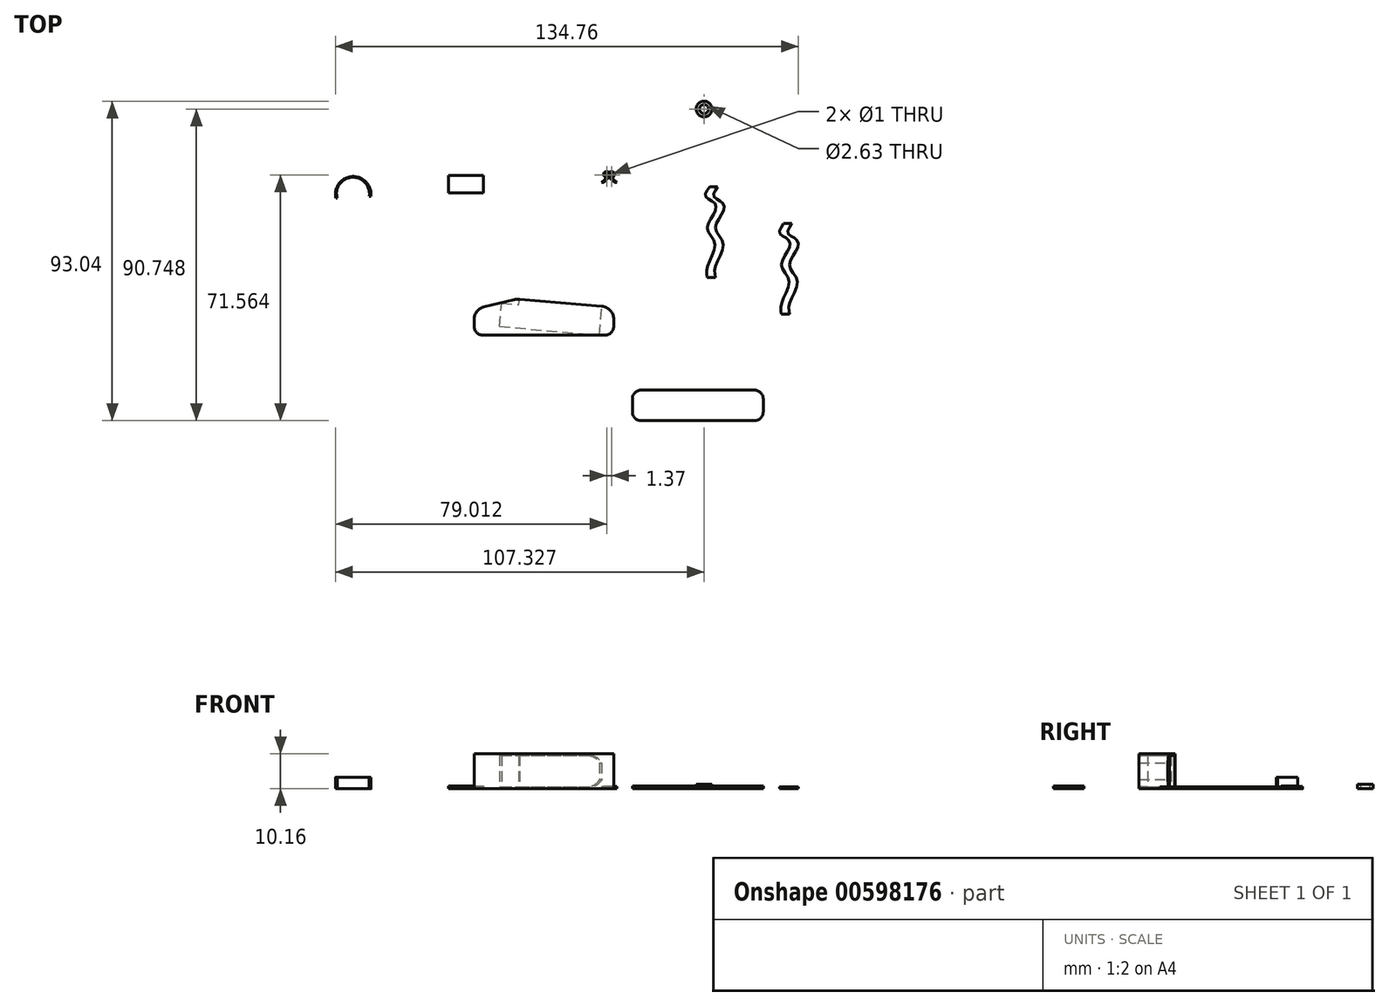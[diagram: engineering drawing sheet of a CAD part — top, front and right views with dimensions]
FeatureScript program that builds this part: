
annotation { "Feature Type Name" : "Feature", "Feature Type Description" : "" }
export const myFeature = defineFeature(function(context is Context, id is Id, definition is map)
    precondition{}
    {
        {
            var Q0;
            Q0=qCreatedBy(makeId("Top.planeOp"),FACE);
            var sketch = newSketch(context, id + "F0", { "sketchPlane" : qUnion([Q0])});
            skLineSegment(sketch, "E0", {"start": v(-27.73, 4.6) * mm, "end": v(-27.73, 2.54) * mm});
            skLineSegment(sketch, "E1", {"start": v(-25.19, 0) * mm, "end": v(10.37, 0) * mm});
            skLineSegment(sketch, "E2", {"start": v(-24.79, 8.3) * mm, "end": v(-16.13, 10.33) * mm});
            skLineSegment(sketch, "E3", {"start": v(-14.55, 10.45) * mm, "end": v(10.76, 8.28) * mm});
            skLineSegment(sketch, "E4", {"start": v(12.91, 4.6) * mm, "end": v(12.91, 2.54) * mm});
            skPoint(sketch, "E5.visualSharp", {"position": v(-27.73, 7.62) * mm});
            skArc(sketch, "E5.filletArc", {"start": v(-24.79, 8.3) * mm, "mid": v(-26.9, 6.97) * mm, "end": v(-27.73, 4.6) * mm});
            skPoint(sketch, "E6.visualSharp", {"position": v(-27.73, 0) * mm});
            skArc(sketch, "E6.filletArc", {"start": v(-27.73, 2.54) * mm, "mid": v(-26.98, 0.74) * mm, "end": v(-25.19, 0) * mm});
            skPoint(sketch, "E7.visualSharp", {"position": v(-15.36, 10.52) * mm});
            skArc(sketch, "E7.filletArc", {"start": v(-14.55, 10.45) * mm, "mid": v(-15.35, 10.45) * mm, "end": v(-16.14, 10.33) * mm});
            skPoint(sketch, "E8.visualSharp", {"position": v(12.91, 8.1) * mm});
            skArc(sketch, "E8.filletArc", {"start": v(12.91, 4.6) * mm, "mid": v(11.9, 7.18) * mm, "end": v(9.43, 8.4) * mm});
            skPoint(sketch, "E9.visualSharp", {"position": v(12.91, 0) * mm});
            skArc(sketch, "E9.filletArc", {"start": v(10.37, 0) * mm, "mid": v(12.17, 0.74) * mm, "end": v(12.91, 2.54) * mm});
            skSolve(sketch);
        }
        {
            var Q0;
            Q0=makeQuery(id+"F0.imprint","IMPRINT",FACE,{"disambiguationData":[TD([[makeQuery(id+"F0.imprint","IMPRINT",EDGE,{"derivedFrom":sQuery(id+"F0.wireOp",EDGE,"E0")}),1.0]])]});
            extrude(context, id + "F1", {"entities" : qUnion([Q0]), "depth" : 10.16 * mm, "offsetDistance" : 25.4 * mm});
        }
        {
            var Q0;
            Q0=makeQuery(id+"F1.opExtrude","SWEPT_FACE",FACE,{"disambiguationData":[OSD([sQuery(id+"F0.wireOp",EDGE,"E3")])]});
            var sketch = newSketch(context, id + "F2", { "sketchPlane" : qUnion([Q0])});
            skLineSegment(sketch, "E10.bottom", {"start": v(15.4, 9.65) * mm, "end": v(-5.25, 9.65) * mm});
            skLineSegment(sketch, "E10.top", {"start": v(15.4, 0.5) * mm, "end": v(-5.25, 0.5) * mm});
            skLineSegment(sketch, "E10.left", {"start": v(15.4, 9.65) * mm, "end": v(15.4, 0.5) * mm});
            skLineSegment(sketch, "E10.right", {"start": v(-9.06, 5.84) * mm, "end": v(-9.06, 4.32) * mm});
            skPoint(sketch, "E11.visualSharp", {"position": v(-9.06, 9.65) * mm});
            skArc(sketch, "E11.filletArc", {"start": v(-5.25, 9.65) * mm, "mid": v(-7.95, 8.54) * mm, "end": v(-9.06, 5.84) * mm});
            skPoint(sketch, "E12.visualSharp", {"position": v(-9.06, 0.5) * mm});
            skArc(sketch, "E12.filletArc", {"start": v(-9.06, 4.32) * mm, "mid": v(-7.95, 1.62) * mm, "end": v(-5.25, 0.5) * mm});
            skPoint(sketch, "E13.visualSharp", {"position": v(15.4, 0.5) * mm});
            skLineSegment(sketch, "E13.filletArc", {"start": v(15.4, 0.5) * mm, "end": v(15.4, 0.5) * mm});
            skPoint(sketch, "E14.visualSharp", {"position": v(15.4, 9.65) * mm});
            skLineSegment(sketch, "E14.filletArc", {"start": v(15.4, 9.65) * mm, "end": v(15.4, 9.65) * mm});
            skSolve(sketch);
        }
        {
            var Q0;
            {var subQ1=sQuery(id+"F2.wireOp",EDGE,"E10.bottom");Q0=makeQuery(id+"F2.imprint","IMPRINT",FACE,{"disambiguationData":[TD([[makeQuery(id+"F2.imprint","IMPRINT",EDGE,{"derivedFrom":subQ1}),1.0]])]});}
            extrude(context, id + "F3", {"entities" : qUnion([Q0]), "operationType" : NewBodyOperationType.REMOVE, "oppositeDirection" : true, "depth" : 8.38 * mm, "offsetDistance" : 25.4 * mm});
        }
        {
            var Q0;
            Q0=makeQuery(id+"F3.boolean.opBoolean","COPY",FACE,{"derivedFrom":makeQuery(id+"F3.opExtrude","SWEPT_FACE",FACE,{"disambiguationData":[OSD([sQuery(id+"F2.wireOp",EDGE,"E10.left")])]})});
            var sketch = newSketch(context, id + "F4", { "sketchPlane" : qUnion([Q0])});
            skLineSegment(sketch, "E15.bottom", {"start": v(7.63, 9.65) * mm, "end": v(0.79, 9.65) * mm});
            skLineSegment(sketch, "E15.top", {"start": v(7.63, 0.5) * mm, "end": v(0.79, 0.5) * mm});
            skLineSegment(sketch, "E15.left", {"start": v(7.63, 9.65) * mm, "end": v(7.63, 0.5) * mm});
            skLineSegment(sketch, "E15.right", {"start": v(0.79, 9.65) * mm, "end": v(0.79, 0.5) * mm});
            skSolve(sketch);
        }
        {
            var Q0;
            Q0=makeQuery(id+"F4.imprint","IMPRINT",FACE,{"disambiguationData":[TD([[makeQuery(id+"F4.imprint","IMPRINT",EDGE,{"derivedFrom":sQuery(id+"F4.wireOp",EDGE,"E15.bottom")}),-1.0]])]});
            extrude(context, id + "F5", {"entities" : qUnion([Q0]), "operationType" : NewBodyOperationType.REMOVE, "oppositeDirection" : true, "depth" : 5.08 * mm, "offsetDistance" : 25.4 * mm});
        }
        {
            var Q0;
            Q0=qCreatedBy(makeId("Top.planeOp"),FACE);
            var sketch = newSketch(context, id + "F6", { "sketchPlane" : qUnion([Q0])});
            skLineSegment(sketch, "E16.bottom", {"start": v(10.9, 47.63) * mm, "end": v(10.9, 47.63) * mm});
            skLineSegment(sketch, "E16.top", {"start": v(9.33, 44.42) * mm, "end": v(9.96, 44.42) * mm});
            skPoint(sketch, "E17.visualSharp", {"position": v(8.19, 47.63) * mm});
            skArc(sketch, "E17.filletArc", {"start": v(10.9, 47.63) * mm, "mid": v(10.66, 47.6) * mm, "end": v(10.44, 47.54) * mm});
            skLineSegment(sketch, "E18", {"start": v(9.96, 44.42) * mm, "end": v(11.58, 46.06) * mm});
            skLineSegment(sketch, "E19", {"start": v(9.33, 44.42) * mm, "end": v(10.33, 45.43) * mm});
            skLineSegment(sketch, "E20", {"start": v(10.3, 46.17) * mm, "end": v(10.21, 46.25) * mm});
            skPoint(sketch, "E21.visualSharp", {"position": v(9.67, 46.72) * mm});
            skArc(sketch, "E21.filletArc", {"start": v(10.44, 47.54) * mm, "mid": v(9.96, 46.96) * mm, "end": v(10.21, 46.25) * mm});
            skPoint(sketch, "E22.visualSharp", {"position": v(10.71, 45.82) * mm});
            skArc(sketch, "E22.filletArc", {"start": v(10.33, 45.43) * mm, "mid": v(10.48, 45.81) * mm, "end": v(10.3, 46.17) * mm});
            skPoint(sketch, "E23.visualSharp", {"position": v(11.45, 47.63) * mm});
            skArc(sketch, "E23.filletArc", {"start": v(11.58, 47.36) * mm, "mid": v(11.26, 47.56) * mm, "end": v(10.9, 47.63) * mm});
            skCircle(sketch, "E24", {"center": v(10.9, 46.66) * mm, "radius": 0.5 * mm});
            skArc(sketch, "E25.MirrorCS", {"start": v(12.26, 47.63) * mm, "mid": v(12.5, 47.6) * mm, "end": v(12.72, 47.54) * mm});
            skArc(sketch, "E26.MirrorCS", {"start": v(11.58, 47.36) * mm, "mid": v(11.9, 47.56) * mm, "end": v(12.26, 47.63) * mm});
            skArc(sketch, "E27.MirrorCS", {"start": v(12.72, 47.54) * mm, "mid": v(13.2, 46.96) * mm, "end": v(12.94, 46.25) * mm});
            skLineSegment(sketch, "E28.MirrorCS", {"start": v(12.85, 46.17) * mm, "end": v(12.94, 46.25) * mm});
            skCircle(sketch, "E29.MirrorC", {"center": v(12.26, 46.66) * mm, "radius": 0.5 * mm});
            skLineSegment(sketch, "E30.MirrorCS", {"start": v(13.82, 44.42) * mm, "end": v(12.82, 45.43) * mm});
            skLineSegment(sketch, "E31.MirrorCS", {"start": v(13.2, 44.42) * mm, "end": v(11.58, 46.06) * mm});
            skLineSegment(sketch, "E32.MirrorCS", {"start": v(13.82, 44.42) * mm, "end": v(13.2, 44.42) * mm});
            skArc(sketch, "E33.MirrorCS", {"start": v(12.82, 45.43) * mm, "mid": v(12.68, 45.81) * mm, "end": v(12.85, 46.17) * mm});
            skSolve(sketch);
        }
        {
            var Q0;
            Q0=makeQuery(id+"F6.imprint","IMPRINT",FACE,{"disambiguationData":[TD([[makeQuery(id+"F6.imprint","IMPRINT",EDGE,{"derivedFrom":sQuery(id+"F6.wireOp",EDGE,"E16.top")}),1.0]])]});
            extrude(context, id + "F7", {"entities" : qUnion([Q0]), "depth" : 0.64 * mm, "offsetDistance" : 25.4 * mm});
        }
        {
            var Q0;
            Q0=qCreatedBy(makeId("Top.planeOp"),FACE);
            var sketch = newSketch(context, id + "F8", { "sketchPlane" : qUnion([Q0])});
            skArc(sketch, "E34", {"start": v(-57.83, 40.38) * mm, "mid": v(-63.18, 46.21) * mm, "end": v(-68, 39.93) * mm});
            skArc(sketch, "E35", {"start": v(-58.3, 40.38) * mm, "mid": v(-63.24, 45.97) * mm, "end": v(-67.63, 39.93) * mm});
            skLineSegment(sketch, "E36", {"start": v(-68, 39.93) * mm, "end": v(-67.63, 39.93) * mm});
            skLineSegment(sketch, "E37", {"start": v(-58.3, 40.38) * mm, "end": v(-57.83, 40.38) * mm});
            skSolve(sketch);
        }
        {
            var Q0;
            Q0=makeQuery(id+"F8.imprint","IMPRINT",FACE,{"disambiguationData":[TD([[makeQuery(id+"F8.imprint","IMPRINT",EDGE,{"derivedFrom":sQuery(id+"F8.wireOp",EDGE,"E34")}),1.0]])]});
            extrude(context, id + "F9", {"entities" : qUnion([Q0]), "depth" : 3.3 * mm, "offsetDistance" : 25.4 * mm});
        }
        {
            var Q0;
            Q0=qCreatedBy(makeId("Top.planeOp"),FACE);
            var sketch = newSketch(context, id + "F10", { "sketchPlane" : qUnion([Q0])});
            skFitSpline(sketch, "E38", {"points": [v(40.82, 43.27) * mm, v(39.71, 40.38) * mm, v(42.15, 38.6) * mm, v(42.37, 35.94) * mm, v(40.15, 31.06) * mm, v(42.37, 26.62) * mm, v(40.15, 19.96) * mm, v(40.15, 16.86) * mm], "startDerivative": vector(-17.53, -25.97) * mm, "endDerivative": vector(4.73, -22) * mm});
            skFitSpline(sketch, "E39", {"points": [v(43.2, 43.27) * mm, v(42.09, 40.38) * mm, v(44.53, 38.6) * mm, v(44.75, 35.94) * mm, v(42.53, 31.06) * mm, v(44.75, 26.62) * mm, v(42.53, 19.96) * mm, v(42.53, 16.86) * mm], "startDerivative": vector(-17.53, -25.97) * mm, "endDerivative": vector(4.73, -22) * mm});
            skLineSegment(sketch, "E40", {"start": v(40.82, 43.27) * mm, "end": v(43.2, 43.27) * mm});
            skLineSegment(sketch, "E41", {"start": v(40.15, 16.86) * mm, "end": v(42.53, 16.86) * mm});
            skFitSpline(sketch, "E42", {"points": [v(62.4, 32.5) * mm, v(61.28, 29.61) * mm, v(63.73, 27.84) * mm, v(63.95, 25.17) * mm, v(61.73, 20.3) * mm, v(63.95, 15.85) * mm, v(61.73, 9.2) * mm, v(61.73, 6.09) * mm], "startDerivative": vector(-17.53, -25.97) * mm, "endDerivative": vector(4.73, -22) * mm});
            skFitSpline(sketch, "E43", {"points": [v(64.77, 32.5) * mm, v(63.66, 29.61) * mm, v(66.1, 27.84) * mm, v(66.33, 25.17) * mm, v(64.1, 20.3) * mm, v(66.33, 15.85) * mm, v(64.1, 9.2) * mm, v(64.1, 6.09) * mm], "startDerivative": vector(-17.53, -25.97) * mm, "endDerivative": vector(4.73, -22) * mm});
            skLineSegment(sketch, "E44", {"start": v(62.4, 32.5) * mm, "end": v(64.77, 32.5) * mm});
            skLineSegment(sketch, "E45", {"start": v(61.73, 6.09) * mm, "end": v(64.1, 6.09) * mm});
            skSolve(sketch);
        }
        {
            var Q0;
            Q0=makeQuery(id+"F10.imprint","IMPRINT",FACE,{"disambiguationData":[TD([[makeQuery(id+"F10.imprint","IMPRINT",EDGE,{"derivedFrom":sQuery(id+"F10.wireOp",EDGE,"E38")}),1.0]])]});
            extrude(context, id + "F11", {"entities" : qUnion([Q0]), "depth" : 0.5 * mm, "offsetDistance" : 25.4 * mm});
        }
        {
            var Q0;
            Q0 = qSketchRegion(id + "F10", true);
            extrude(context, id + "F12", {"entities" : qUnion([Q0]), "operationType" : NewBodyOperationType.ADD, "depth" : 0.5 * mm, "offsetDistance" : 25.4 * mm});
        }
        {
            var Q0;
            Q0=qCreatedBy(makeId("Top.planeOp"),FACE);
            var sketch = newSketch(context, id + "F13", { "sketchPlane" : qUnion([Q0])});
            skLineSegment(sketch, "E46.bottom", {"start": v(20.87, -16) * mm, "end": v(53.9, -16) * mm});
            skLineSegment(sketch, "E46.top", {"start": v(20.87, -24.9) * mm, "end": v(53.9, -24.9) * mm});
            skLineSegment(sketch, "E46.left", {"start": v(18.33, -18.55) * mm, "end": v(18.33, -22.36) * mm});
            skLineSegment(sketch, "E46.right", {"start": v(56.43, -18.55) * mm, "end": v(56.43, -22.36) * mm});
            skPoint(sketch, "E46.middle", {"position": v(37.38, -20.45) * mm});
            skPoint(sketch, "E47.visualSharp", {"position": v(18.33, -16) * mm});
            skArc(sketch, "E47.filletArc", {"start": v(20.87, -16) * mm, "mid": v(19.08, -16.75) * mm, "end": v(18.33, -18.55) * mm});
            skPoint(sketch, "E48.visualSharp", {"position": v(18.33, -24.9) * mm});
            skArc(sketch, "E48.filletArc", {"start": v(18.33, -22.36) * mm, "mid": v(19.08, -24.16) * mm, "end": v(20.87, -24.9) * mm});
            skPoint(sketch, "E49.visualSharp", {"position": v(56.43, -16) * mm});
            skArc(sketch, "E49.filletArc", {"start": v(56.43, -18.55) * mm, "mid": v(55.7, -16.75) * mm, "end": v(53.9, -16) * mm});
            skPoint(sketch, "E50.visualSharp", {"position": v(56.43, -24.9) * mm});
            skArc(sketch, "E50.filletArc", {"start": v(53.9, -24.9) * mm, "mid": v(55.7, -24.16) * mm, "end": v(56.43, -22.36) * mm});
            skSolve(sketch);
        }
        {
            var Q0;
            Q0=makeQuery(id+"F13.imprint","IMPRINT",FACE,{"disambiguationData":[TD([[makeQuery(id+"F13.imprint","IMPRINT",EDGE,{"derivedFrom":sQuery(id+"F13.wireOp",EDGE,"E46.bottom")}),-1.0]])]});
            extrude(context, id + "F14", {"entities" : qUnion([Q0]), "depth" : 0.76 * mm, "offsetDistance" : 25.4 * mm});
        }
        {
            var Q0;
            Q0=qCreatedBy(makeId("Top.planeOp"),FACE);
            var sketch = newSketch(context, id + "F15", { "sketchPlane" : qUnion([Q0])});
            skCircle(sketch, "E51", {"center": v(39.2, 65.85) * mm, "radius": 2.3 * mm});
            skCircle(sketch, "E52", {"center": v(39.2, 65.85) * mm, "radius": 1.32 * mm});
            skSolve(sketch);
        }
        {
            var Q0;
            Q0 = qSketchRegion(id + "F15", true);
            extrude(context, id + "F16", {"entities" : qUnion([Q0]), "depth" : 1.27 * mm, "offsetDistance" : 25.4 * mm});
        }
        {
            var Q0;
            Q0=qCreatedBy(makeId("Top.planeOp"),FACE);
            var sketch = newSketch(context, id + "F17", { "sketchPlane" : qUnion([Q0])});
            skLineSegment(sketch, "E53.bottom", {"start": v(-35.23, 46.5) * mm, "end": v(-25.07, 46.5) * mm});
            skLineSegment(sketch, "E53.top", {"start": v(-35.23, 41.43) * mm, "end": v(-25.07, 41.43) * mm});
            skLineSegment(sketch, "E53.left", {"start": v(-35.23, 46.5) * mm, "end": v(-35.23, 41.43) * mm});
            skLineSegment(sketch, "E53.right", {"start": v(-25.07, 46.5) * mm, "end": v(-25.07, 41.43) * mm});
            skPoint(sketch, "E53.middle", {"position": v(-30.15, 43.97) * mm});
            skSolve(sketch);
        }
        {
            var Q0;
            Q0=makeQuery(id+"F17.imprint","IMPRINT",FACE,{"disambiguationData":[TD([[makeQuery(id+"F17.imprint","IMPRINT",EDGE,{"derivedFrom":sQuery(id+"F17.wireOp",EDGE,"E53.bottom")}),-1.0]])]});
            extrude(context, id + "F18", {"entities" : qUnion([Q0]), "depth" : 0.76 * mm, "offsetDistance" : 25.4 * mm});
        }
    });
